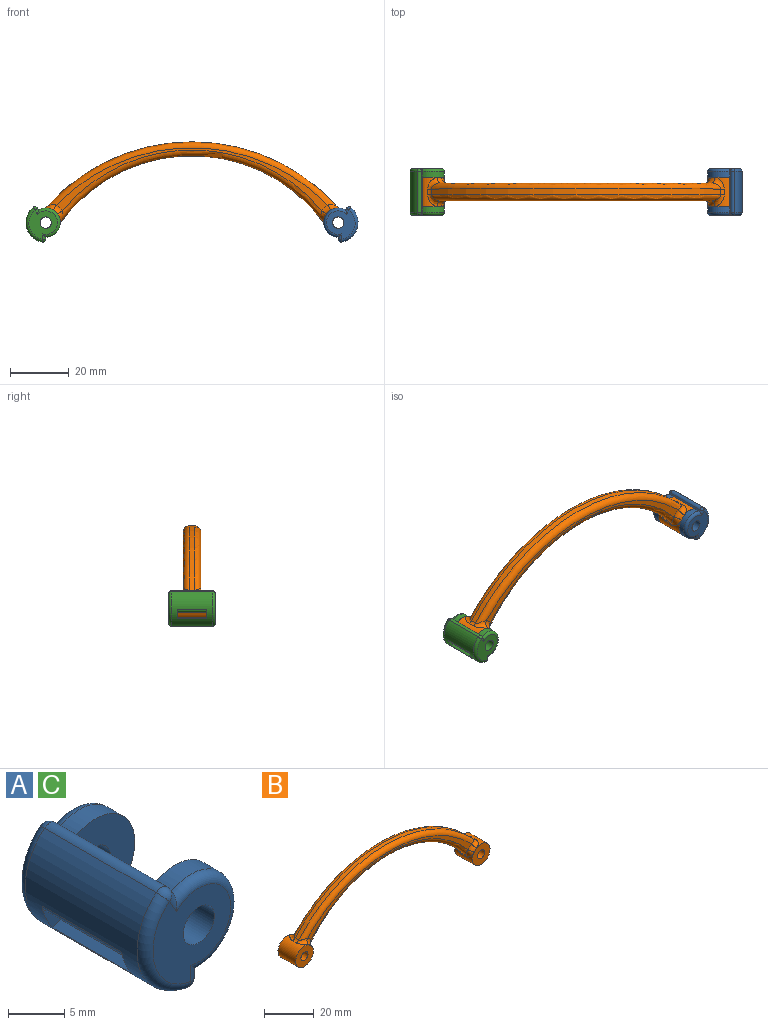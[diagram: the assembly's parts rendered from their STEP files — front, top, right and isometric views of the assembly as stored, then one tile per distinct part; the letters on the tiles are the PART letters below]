
ASSEMBLY  parts=3 mates=1
PART A: 32 faces, bbox 12.7x16x12.8 mm
  f0: cylinder r=6.75mm len=14.02mm, axis (0,-1,0), area 180.7mm2, adj f12,f13,f15,f16,f17,f20,f26,f30
  f1: cylinder r=5mm len=10.02mm, axis (0,-1,0), area 104.1mm2, adj f2,f4,f6,f8,f13,f14,f15,f31
  f2: plane 10x10mm, normal (0,1,0), area 66.6mm2, adj f1,f3,f5
  f3: cylinder r=5mm len=10mm, axis (0,-1,0), area 36.7mm2, adj f2,f4,f6,f27
  f4: plane 14.02x0.57mm, normal (0.87,0,0.5), area 9.3mm2, adj f1,f3,f9,f16,f23,f29
  f5: cylinder r=1.95mm len=3.9mm, axis (0,-1,0), area 36.8mm2, adj f2,f7
  f6: plane 14.02x0.66mm, normal (1,0,0), area 9.3mm2, adj f1,f3,f9,f17,f19,f25
  f7: plane 10.07x9.75mm, normal (0,-1,0), area 57.1mm2, adj f5,f25,f26,f27,f29
  f8: plane 10x10mm, normal (0,-1,0), area 66.6mm2, adj f1,f9,f10
  f9: cylinder r=5mm len=10mm, axis (0,-1,0), area 36.7mm2, adj f4,f6,f8,f21
  f10: cylinder r=1.95mm len=3.9mm, axis (0,-1,0), area 36.8mm2, adj f8,f11
  f11: plane 10.07x9.75mm, normal (0,1,0), area 57.1mm2, adj f10,f19,f20,f21,f23
  f12: plane 10x0.88mm, normal (-0.5,0,0.87), area 10.2mm2, adj f0,f13,f15,f31
  f13: plane 3.41x3.07mm, normal (0,-1,0), area 4mm2, adj f0,f1,f12,f14,f30,f31
  f14: plane 10x0.43mm, normal (0.5,0,-0.87), area 4.9mm2, adj f1,f13,f15,f30
  f15: plane 3.41x3.07mm, normal (0,1,0), area 4mm2, adj f0,f1,f12,f14,f30,f31
  f16: cylinder r=1mm len=14.02mm, axis (0,-1,0), area 24.5mm2, adj f0,f4,f22,f28
  f17: cylinder r=1mm len=14.02mm, axis (0,-1,0), area 24.5mm2, adj f0,f6,f18,f24
  f18: sphere r=1mm, area 1.7mm2, adj f17,f19,f20
  f19: cylinder r=1mm len=1.79mm, axis (0,0,1), area 1.7mm2, adj f6,f11,f18,f21
  f20: torus R=5.75mm, axis (0,1,0), area 22.8mm2, adj f0,f11,f18,f22
  f21: torus R=4mm, axis (0,1,0), area 27.8mm2, adj f9,f11,f19,f23
  f22: sphere r=1mm, area 1.7mm2, adj f16,f20,f23
  f23: cylinder r=1mm len=2.05mm, axis (-0.5,0,0.87), area 1.7mm2, adj f4,f11,f21,f22
  f24: sphere r=1mm, area 1.7mm2, adj f17,f25,f26
  f25: cylinder r=1mm len=1.79mm, axis (0,0,1), area 1.7mm2, adj f6,f7,f24,f27
  f26: torus R=5.75mm, axis (0,-1,0), area 22.8mm2, adj f0,f7,f24,f28
  f27: torus R=4mm, axis (0,-1,0), area 27.8mm2, adj f3,f7,f25,f29
  f28: sphere r=1mm, area 1.7mm2, adj f16,f26,f29
  f29: cylinder r=1mm len=2.05mm, axis (-0.5,0,0.87), area 1.7mm2, adj f4,f7,f27,f28
  f30: cylinder r=1mm len=10mm, axis (0,-1,0), area 19.3mm2, adj f0,f13,f14,f15
  f31: cylinder r=1mm len=10mm, axis (0,-1,0), area 12.3mm2, adj f1,f12,f13,f15
PART B: 32 faces, bbox 110x12.8x38.1 mm
  f0: cylinder r=55.74mm len=89.28mm, axis (0,1,0), area 207.1mm2, adj f18,f19,f27,f28
  f1: cylinder r=66.6mm len=98.94mm, axis (0,1,0), area 223mm2, adj f15,f16,f25,f26
  f2: plane 92.74x21.5mm, normal (0,-1,0), area 147.2mm2, adj f20,f25,f28,f31
  f3: plane 92.74x21.5mm, normal (0,1,0), area 147.2mm2, adj f12,f16,f17,f18
  f4: cylinder r=2mm len=10mm, axis (0,1,0), area 126mm2, adj f6,f7
  f5: cylinder r=5mm len=10mm, axis (0,1,0), area 237.7mm2, adj f6,f7,f13,f14,f15,f19,f21,f24
  f6: plane 10x10mm, normal (0,-1,0), area 65.9mm2, adj f4,f5,f20
  f7: plane 10x10mm, normal (0,1,0), area 65.9mm2, adj f4,f5,f12
  f8: cylinder r=5mm len=10mm, axis (0,1,0), area 237.7mm2, adj f10,f11,f22,f23,f26,f27,f29,f30
  f9: cylinder r=2mm len=10mm, axis (0,1,0), area 126mm2, adj f10,f11
  f10: plane 10x10mm, normal (0,-1,0), area 65.9mm2, adj f8,f9,f31
  f11: plane 10x10mm, normal (0,1,0), area 65.9mm2, adj f8,f9,f17
  f12: torus R=7mm, axis (0,-1,0), area 7.2mm2, adj f3,f7,f13,f14
  f13: bspline ~4.71x4.67mm, area 9.8mm2, adj f5,f12,f15,f16
  f14: bspline ~4.71x4.5mm, area 9.7mm2, adj f5,f12,f18,f19
  f15: cylinder r=2mm len=2mm, axis (0,-1,0), area 2.8mm2, adj f1,f5,f13,f21
  f16: torus R=64.6mm, axis (0,-1,0), area 339.6mm2, adj f1,f3,f13,f22
  f17: torus R=7mm, axis (0,-1,0), area 7.2mm2, adj f3,f11,f22,f23
  f18: torus R=57.74mm, axis (0,-1,0), area 320.2mm2, adj f0,f3,f14,f23
  f19: cylinder r=2mm len=2mm, axis (0,1,0), area 2.2mm2, adj f0,f5,f14,f24
  f20: torus R=7mm, axis (0,-1,0), area 7.2mm2, adj f2,f6,f21,f24
  f21: bspline ~4.69x4.34mm, area 9.8mm2, adj f5,f15,f20,f25
  f22: bspline ~4.69x4.34mm, area 9.8mm2, adj f8,f16,f17,f26
  f23: bspline ~4.95x4.48mm, area 9.7mm2, adj f8,f17,f18,f27
  f24: bspline ~4.95x4.48mm, area 9.7mm2, adj f5,f19,f20,f28
  f25: torus R=64.6mm, axis (0,-1,0), area 339.6mm2, adj f1,f2,f21,f29
  f26: cylinder r=2mm len=2mm, axis (0,-1,0), area 2.8mm2, adj f1,f8,f22,f29
  f27: cylinder r=2mm len=2mm, axis (0,1,0), area 2.2mm2, adj f0,f8,f23,f30
  f28: torus R=57.74mm, axis (0,-1,0), area 320.2mm2, adj f0,f2,f24,f30
  f29: bspline ~4.71x4.67mm, area 9.8mm2, adj f8,f25,f26,f31
  f30: bspline ~4.71x4.5mm, area 9.7mm2, adj f8,f27,f28,f31
  f31: torus R=7mm, axis (0,-1,0), area 7.2mm2, adj f2,f10,f29,f30
PART C: same geometry as A
PLACE A rot(axis=(0,0,1),180deg) t=(60.32,3.26,8.65)mm
PLACE B t=(10.32,-4.74,8.65)mm
PLACE C rot(axis=(1,0,0),0deg) t=(-39.68,-12.76,8.65)mm
MATE fastened C.f9 <-> B.f5  axis (0,-1,0) through (-39.68,0.26,8.65)mm
